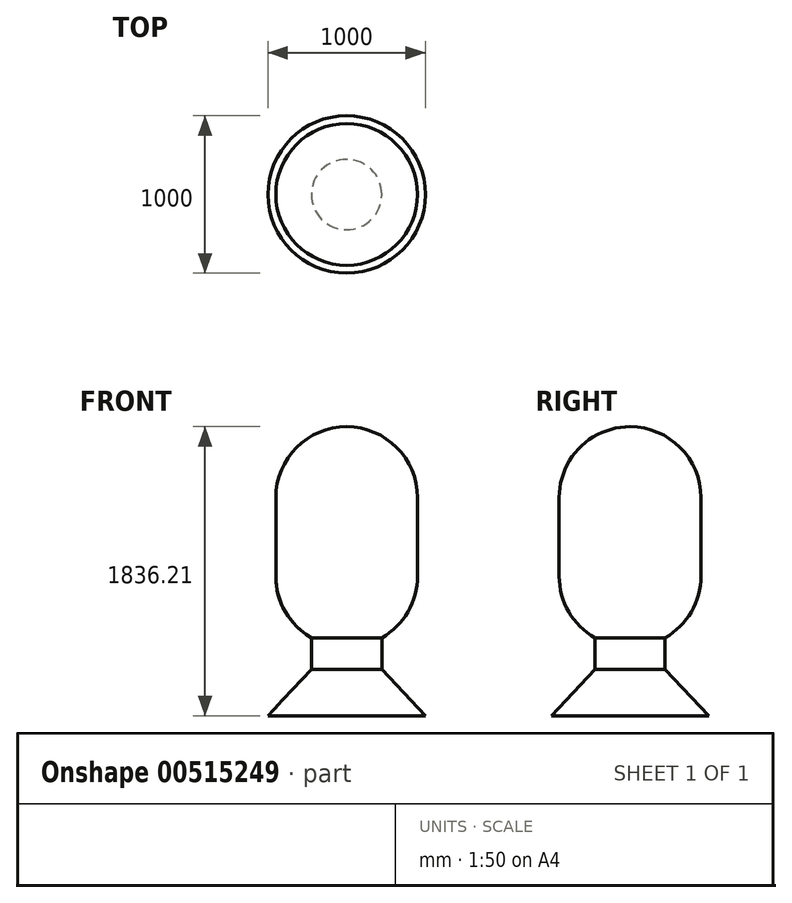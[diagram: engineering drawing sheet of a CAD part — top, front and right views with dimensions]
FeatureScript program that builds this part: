
annotation { "Feature Type Name" : "Feature", "Feature Type Description" : "" }
export const myFeature = defineFeature(function(context is Context, id is Id, definition is map)
    precondition{}
    {
        {
            var Q0;
            Q0=qCreatedBy(makeId("Right.planeOp"),FACE);
            var sketch = newSketch(context, id + "F0", { "sketchPlane" : qUnion([Q0])});
            skLineSegment(sketch, "E0", {"start": v(0, 0) * mm, "end": v(-500, 0) * mm});
            skLineSegment(sketch, "E1", {"start": v(-500, 0) * mm, "end": v(-223.24, 295.49) * mm});
            skLineSegment(sketch, "E2", {"start": v(-450, 886.2) * mm, "end": v(-450, 1386.2) * mm});
            skLineSegment(sketch, "E3", {"start": v(0, 0) * mm, "end": v(0, 2199.22) * mm, "construction": true});
            skArc(sketch, "E4", {"start": v(-450, 1386.2) * mm, "mid": v(-318.2, 1704.4) * mm, "end": v(0, 1836.2) * mm});
            skArc(sketch, "E5", {"start": v(-450, 886.2) * mm, "mid": v(-389.2, 660.33) * mm, "end": v(-223.24, 495.49) * mm});
            skLineSegment(sketch, "E6", {"start": v(-223.24, 495.49) * mm, "end": v(-223.24, 295.49) * mm});
            skLineSegment(sketch, "E7", {"start": v(0, 1836.2) * mm, "end": v(0, 0) * mm});
            skSolve(sketch);
        }
        {
            var Q0;
            Q0=makeQuery(id+"F0.imprint","IMPRINT",FACE,{"disambiguationData":[TD([[makeQuery(id+"F0.imprint","IMPRINT",EDGE,{"derivedFrom":sQuery(id+"F0.wireOp",EDGE,"E0")}),-1.0]])]});
            var Q1;
            Q1=sQuery(id+"F0.wireOp",EDGE,"E3");
            revolve(context, id + "F1", {"entities" : qUnion([Q0]), "axis" : qUnion([Q1]), "revolveType" : RevolveType.FULL});
        }
    });
